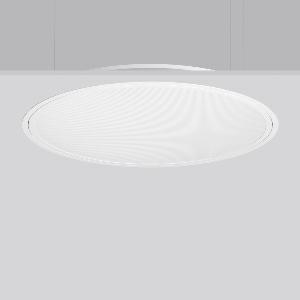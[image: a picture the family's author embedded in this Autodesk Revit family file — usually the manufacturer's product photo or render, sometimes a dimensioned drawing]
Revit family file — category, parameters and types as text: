
# Revit family: triona_round_e_312299_002_12_2d8b
name_source: partatom
category: Lighting Fixtures
units: mm (PartAtom-declared; Revit-internal decimal feet)

## family parameters
Cut with Voids When Loaded = No
Host = Face
Light Source = No
Part Type = Normal
Room Calculation Point = No
Round Connector Dimension = Use Diameter
Shared = No

## types (1)
- TRIONA round E (1 x LED Modul 830, 8050 lm, 3000)
    Apparent Load = 66 VA
    CIE Flux Codes = 59 87 97 100 100
    Color Rendering = 80
    Color Temperature = 3000
    Default Elevation = 1800 mm
    Description = Series: TRIONA round
Decorative round LED recessed surface luminaire. Cover made of sheet steel, powder-coated. Frame made of aluminium, powder-coated. Recessed ring: aluminium extrusion profile, powder coated. Light emission through a diffuser in plastic, opal/prismatic. Lightguide and diffuser made of non-yellowing plastic (PMMA). Lateral light emission (RZB SIDELITE technology) for above-average homogeneous light distribution. Suitable for installation in cavity ceilings. Tool-free mounting system thanks to the rocker arm mechanism (patent pending). Electronic ballast included. Very easy installation thanks to Plug+Play connection. 
Colour: traffic white, matt (RAL 9016)
Diameter: 889 mm
Height: 2 mm
Cut-out diameter: 866 mm
Recess height: 100 mm
Luminaire: recess height: 89 mm
Lamp: LED
Socket: without socket
Colour temperature: 3000K
Colour rendering index (CRI): 80
System power: 66 W
Rated luminous flux: 8050 lm
Luminous efficiency: 122 lm/W
Control gear: Converter, dimmable, DALI
Protection class: I
Type of protection: IP 40
    Height = 0 mm  [stored 0 ft]
    Lamp = 1 x LED Modul 830
    Lamp Light Flux = 8050 lm
    Lamp count = 1
    Length = 889 mm
    Lifetime = 50000 h
    Luminous efficacy = 122 lm/W
    Manufacturer = RZB
    ModVariant = No
    Model = 312299.002.12
    Mounting Place = Ceiling
    Mounting Type = Recessed
    Number of Poles = 1
    OnlyDefault = Yes
    Power Factor = 1
    Product Name = TRIONA round E
    Product group = Recessed modular luminaires
    ProductGroupID = 406
    Protection Class = Protection class I
    Protection Degree = IP 20
    RLX_Detail_Level = 1
    RLX_Emergency_Light_Flux = 0 lm
    RLX_Emergency_Type = 0
    RLX_Emergency_Type_DB = No
    RlxData = <blob elided: 39565 chars, md5=84b73e0a>
    Socket = socket
    Standby Power = 0 W
    System Light Flux = 8050 lm
    System Power = 66 W
    Type Comments = Product without accessories
    Type Image = 312299.002.12.jpg
    URL = http://relux.com
    VarID = ---
    Voltage = 230 V
    Voltage Range = 220-240 V
    Weight = 0.00 kg
    Width = 0 mm  [stored 0 ft]

note: [stored X ft] marks values corroborated as IEEE doubles in the binary element streams (Revit-internal decimal feet)

## geometry (parser evidence)
native form markers: Blend x4, Sweep x10
no freeform markers — native parametric forms only
